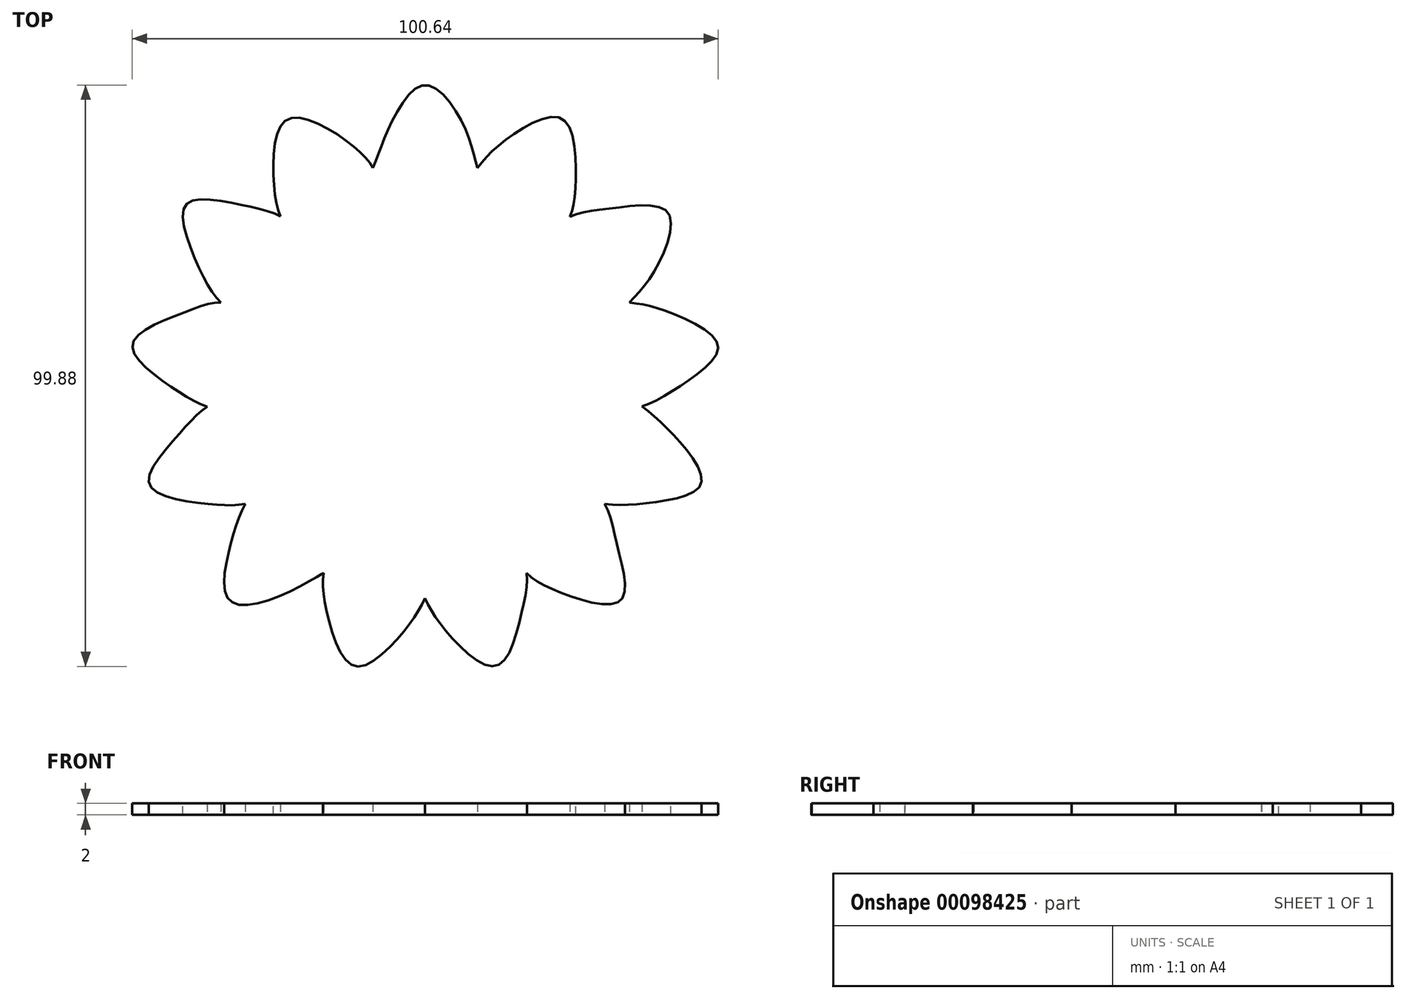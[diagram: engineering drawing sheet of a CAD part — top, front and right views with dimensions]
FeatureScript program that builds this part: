
annotation { "Feature Type Name" : "Feature", "Feature Type Description" : "" }
export const myFeature = defineFeature(function(context is Context, id is Id, definition is map)
    precondition{}
    {
        {
            var Q0;
            Q0=qCreatedBy(makeId("Top.planeOp"),FACE);
            var sketch = newSketch(context, id + "F0", { "sketchPlane" : qUnion([Q0])});
            skPoint(sketch, "E0.center", {"position": v(0, 0) * mm});
            skLineSegment(sketch, "E1", {"start": v(9, 36.4) * mm, "end": v(0, 0) * mm});
            skLineSegment(sketch, "E2.1.0", {"start": v(-8.95, 36.42) * mm, "end": v(0, 0) * mm});
            skLineSegment(sketch, "E2.2.0", {"start": v(-24.85, 28.08) * mm, "end": v(0, 0) * mm});
            skLineSegment(sketch, "E2.3.0", {"start": v(-35.06, 13.32) * mm, "end": v(0, 0) * mm});
            skLineSegment(sketch, "E2.4.0", {"start": v(-37.23, -4.5) * mm, "end": v(0, 0) * mm});
            skLineSegment(sketch, "E2.5.0", {"start": v(-30.87, -21.28) * mm, "end": v(0, 0) * mm});
            skLineSegment(sketch, "E2.6.0", {"start": v(-17.45, -33.2) * mm, "end": v(0, 0) * mm});
            skLineSegment(sketch, "E2.7.0", {"start": v(-0.02, -37.5) * mm, "end": v(0, 0) * mm});
            skLineSegment(sketch, "E2.8.0", {"start": v(17.4, -33.21) * mm, "end": v(0, 0) * mm});
            skLineSegment(sketch, "E2.9.0", {"start": v(30.85, -21.32) * mm, "end": v(0, 0) * mm});
            skLineSegment(sketch, "E2.10.0", {"start": v(37.22, -4.54) * mm, "end": v(0, 0) * mm});
            skLineSegment(sketch, "E2.11.0", {"start": v(35.07, 13.28) * mm, "end": v(0, 0) * mm});
            skLineSegment(sketch, "E2.12.0", {"start": v(24.88, 28.05) * mm, "end": v(0, 0) * mm});
            skFitSpline(sketch, "E3", {"points": [v(-8.95, 36.42) * mm, v(-6.03, 43.69) * mm, v(0, 50.64) * mm, v(6.6, 43.7) * mm, v(9, 36.4) * mm], "startDerivative": vector(11.1, 27.19) * mm, "endDerivative": vector(7.13, -25.52) * mm});
            skFitSpline(sketch, "E4", {"points": [v(9, 36.4) * mm, v(14.38, 41.65) * mm, v(23.53, 44.84) * mm, v(25.88, 34.78) * mm, v(24.88, 28.05) * mm], "startDerivative": vector(15.71, 21.62) * mm, "endDerivative": vector(-9.9, -21.73) * mm});
            skFitSpline(sketch, "E5", {"points": [v(24.88, 28.05) * mm, v(32.2, 29.5) * mm, v(41.67, 28.76) * mm, v(39.68, 19.22) * mm, v(35.07, 13.28) * mm], "startDerivative": vector(24.68, 11.79) * mm, "endDerivative": vector(-19.61, -21.08) * mm});
            skFitSpline(sketch, "E6", {"points": [v(35.07, 13.28) * mm, v(41, 11.94) * mm, v(50.27, 6.1) * mm, v(45.3, -0.03) * mm, v(37.22, -4.54) * mm], "startDerivative": vector(29.39, -3.26) * mm, "endDerivative": vector(-26.64, -8.2) * mm});
            skFitSpline(sketch, "E7", {"points": [v(37.22, -4.54) * mm, v(43.5, -10.36) * mm, v(47.34, -17.96) * mm, v(39.02, -21.06) * mm, v(30.85, -21.32) * mm], "startDerivative": vector(24.85, -18.82) * mm, "endDerivative": vector(-29.44, 3.84) * mm});
            skFitSpline(sketch, "E8", {"points": [v(30.85, -21.32) * mm, v(33.18, -29.27) * mm, v(33.58, -37.9) * mm, v(23.92, -36.8) * mm, v(17.4, -33.21) * mm], "startDerivative": vector(13.8, -25.64) * mm, "endDerivative": vector(-17.96, 17.15) * mm});
            skFitSpline(sketch, "E9", {"points": [v(17.4, -33.21) * mm, v(16.36, -40.84) * mm, v(12.12, -49.16) * mm, v(3.73, -43.31) * mm, v(-0.02, -37.5) * mm], "startDerivative": vector(3.4, -25.66) * mm, "endDerivative": vector(-11.9, 25.45) * mm});
            skFitSpline(sketch, "E10", {"points": [v(-0.02, -37.5) * mm, v(-4.06, -43.68) * mm, v(-12.12, -49.16) * mm, v(-16.82, -40.1) * mm, v(-17.45, -33.2) * mm], "startDerivative": vector(-11.14, -25.2) * mm, "endDerivative": vector(3.69, 24.82) * mm});
            skFitSpline(sketch, "E11", {"points": [v(-17.44, -33.22) * mm, v(-17.45, -33.2) * mm, v(-23.76, -36.63) * mm, v(-33.58, -37.9) * mm, v(-33.66, -29.2) * mm, v(-30.87, -21.28) * mm], "startDerivative": vector(0.21, 2.29) * mm, "endDerivative": vector(14.32, 25.76) * mm});
            skFitSpline(sketch, "E12", {"points": [v(-30.87, -21.28) * mm, v(-37.62, -21.27) * mm, v(-47.34, -17.96) * mm, v(-42.33, -9.39) * mm, v(-37.23, -4.5) * mm], "startDerivative": vector(-27, -5.31) * mm, "endDerivative": vector(23.54, 13.78) * mm});
            skFitSpline(sketch, "E13", {"points": [v(-37.18, -4.7) * mm, v(-44.31, -0.72) * mm, v(-50.27, 6.1) * mm, v(-41.83, 11.41) * mm, v(-35.06, 13.32) * mm], "startDerivative": vector(-25.66, 8.05) * mm, "endDerivative": vector(25.1, -0.57) * mm});
            skFitSpline(sketch, "E14", {"points": [v(-35.06, 13.32) * mm, v(-39.2, 20.06) * mm, v(-41.12, 30.06) * mm, v(-32.42, 30.23) * mm, v(-24.85, 28.08) * mm], "startDerivative": vector(-19.32, 17.01) * mm, "endDerivative": vector(21.34, -12.16) * mm});
            skFitSpline(sketch, "E15", {"points": [v(-24.85, 28.08) * mm, v(-26.06, 36.45) * mm, v(-23.53, 44.84) * mm, v(-13.82, 41.28) * mm, v(-8.95, 36.42) * mm], "startDerivative": vector(-9.8, 21.68) * mm, "endDerivative": vector(10.93, -19.75) * mm});
            skSolve(sketch);
        }
        {
            var Q0;
            Q0 = qSketchRegion(id + "F0", true);
            extrude(context, id + "F1", {"entities" : qUnion([Q0]), "depth" : 2 * mm});
        }
        {
            var Q0;
            Q0=makeQuery(id+"F1.opExtrude","SWEPT_BODY",BODY,{"disambiguationData":[OSD([sQuery(id+"F0.wireOp",EDGE,"E3"),sQuery(id+"F0.wireOp",EDGE,"E4"),sQuery(id+"F0.wireOp",EDGE,"E5"),sQuery(id+"F0.wireOp",EDGE,"E6"),sQuery(id+"F0.wireOp",EDGE,"E7"),sQuery(id+"F0.wireOp",EDGE,"E8"),sQuery(id+"F0.wireOp",EDGE,"E9"),sQuery(id+"F0.wireOp",EDGE,"E10"),sQuery(id+"F0.wireOp",EDGE,"E11"),sQuery(id+"F0.wireOp",EDGE,"E12"),sQuery(id+"F0.wireOp",EDGE,"E13"),sQuery(id+"F0.wireOp",EDGE,"E14"),sQuery(id+"F0.wireOp",EDGE,"E15")])]});
            transform(context, id + "F2", {"entities" : qUnion([Q0]), "transformType" : TransformType.TRANSLATION_3D, "dx" : 0 * mm, "dy" : 0 * mm, "dz" : 0 * mm, "makeCopy" : true});
        }
    });
